# Revit family: Access_Door-Hidden_Flange-Best Access Doors-Removable-BA-RHF
name_source: partatom
category: Specialty Equipment
revit_build: Autodesk Revit 2017 (Build: 20160225_1515(x64)
units: mm (PartAtom-declared; Revit-internal decimal feet)

## family parameters
Cut with Voids When Loaded = No
Host = Face
OmniClass Number = 23.30.10.27.17
Part Type = Normal
Room Calculation Point = No
Round Connector Dimension = Use Diameter
Shared = No

## types (5) — shared parameters
Assembly Code = C1020700
Construction Material = Metal - Best Access Doors - Aluminum
Default Elevation = 0"
Description = Removable aesthetic access door with hidden flange
Finish = Metal - Best Access Doors - Powder Coated White
Frame Depth = 1 15/32"
Manufacturer = Best Access Doors
Model = BA-RHF
Product data url = https://bimobject.com
URL = https://www.bestaccessdoors.com

## per-type parameters (varying)
| type | Door Height | Door Width | Frame Height Calc | Frame Width Calc | Height Actual | Width Actual |
| Custom | 24" | 24" | 24" | 24" | 24" | 24" |
| 8 x 8 | 8" | 8" | 8" | 8" | 8" | 8" |
| 12 x 12 | 12" | 12" | 12" | 12" | 12" | 12" |
| 16 x 16 | 16" | 16" | 16" | 16" | 16" | 16" |
| 24 x 24 | 24" | 24" | 24" | 24" | 24" | 24" |

## geometry (parser evidence)
native form markers: Blend x4, Sweep x10
no freeform markers — native parametric forms only
